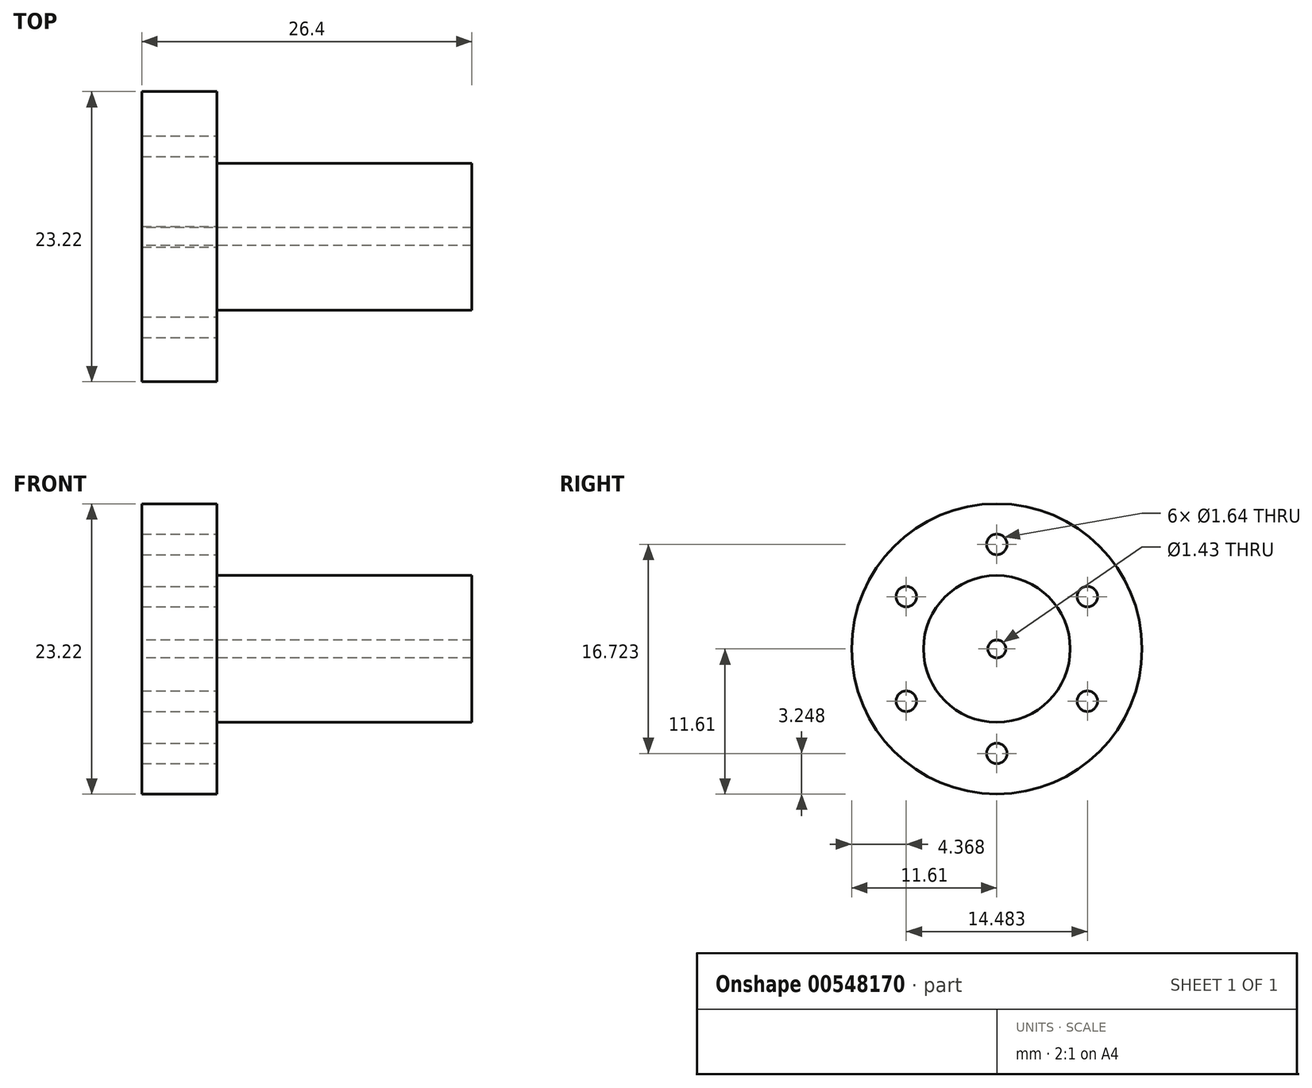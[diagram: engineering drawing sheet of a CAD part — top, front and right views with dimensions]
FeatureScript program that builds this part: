
annotation { "Feature Type Name" : "Feature", "Feature Type Description" : "" }
export const myFeature = defineFeature(function(context is Context, id is Id, definition is map)
    precondition{}
    {
        {
            var Q0;
            Q0=qCreatedBy(makeId("Front.planeOp"),FACE);
            var sketch = newSketch(context, id + "F0", { "sketchPlane" : qUnion([Q0])});
            skLineSegment(sketch, "E0", {"start": v(-9.4, 11.6) * mm, "end": v(-9.4, 0.72) * mm});
            skLineSegment(sketch, "E1", {"start": v(-9.4, 0.72) * mm, "end": v(17, 0.72) * mm});
            skLineSegment(sketch, "E2", {"start": v(17, 0.72) * mm, "end": v(17, 5.87) * mm});
            skLineSegment(sketch, "E3", {"start": v(17, 5.87) * mm, "end": v(-3.4, 5.87) * mm});
            skLineSegment(sketch, "E4", {"start": v(-3.4, 5.87) * mm, "end": v(-3.4, 11.6) * mm});
            skLineSegment(sketch, "E5", {"start": v(-3.4, 11.6) * mm, "end": v(-9.4, 11.6) * mm});
            skLineSegment(sketch, "E6", {"start": v(-18.4, 0) * mm, "end": v(18.59, 0) * mm, "construction": true});
            skSolve(sketch);
        }
        {
            var Q0;
            Q0 = qSketchRegion(id + "F0", true);
            var Q1;
            Q1=sQuery(id+"F0.wireOp",EDGE,"E6");
            revolve(context, id + "F1", {"entities" : qUnion([Q0]), "axis" : qUnion([Q1]), "revolveType" : RevolveType.FULL});
        }
        {
            var Q0;
            Q0=makeQuery(id+"F1.opRevolve","SWEPT_FACE",FACE,{"disambiguationData":[OSD([sQuery(id+"F0.wireOp",EDGE,"E2")])]});
            var sketch = newSketch(context, id + "F2", { "sketchPlane" : qUnion([Q0])});
            skSolve(sketch);
        }
        {
            var Q0;
            Q0=makeQuery(id+"F1.opRevolve","SWEPT_FACE",FACE,{"disambiguationData":[OSD([sQuery(id+"F0.wireOp",EDGE,"E4")])]});
            var sketch = newSketch(context, id + "F3", { "sketchPlane" : qUnion([Q0])});
            skLineSegment(sketch, "E7", {"start": v(0, 0) * mm, "end": v(0, 12.55) * mm, "construction": true});
            skCircle(sketch, "E8", {"center": v(0, 8.36) * mm, "radius": 0.82 * mm});
            skCircle(sketch, "E9.1.0", {"center": v(7.24, 4.18) * mm, "radius": 0.82 * mm});
            skCircle(sketch, "E9.2.0", {"center": v(7.24, -4.18) * mm, "radius": 0.82 * mm});
            skCircle(sketch, "E9.3.0", {"center": v(0, -8.36) * mm, "radius": 0.82 * mm});
            skCircle(sketch, "E9.4.0", {"center": v(-7.24, -4.18) * mm, "radius": 0.82 * mm});
            skCircle(sketch, "E9.5.0", {"center": v(-7.24, 4.18) * mm, "radius": 0.82 * mm});
            skPoint(sketch, "E9.center", {"position": v(0, 0) * mm});
            skLineSegment(sketch, "E9.anchor1", {"start": v(0, 0) * mm, "end": v(0, 8.36) * mm, "construction": true});
            skLineSegment(sketch, "E9.anchor2", {"start": v(0, 0) * mm, "end": v(-7.24, 4.18) * mm, "construction": true});
            skSolve(sketch);
        }
        {
            var Q0;
            Q0=makeQuery(id+"F3.imprint","IMPRINT",FACE,{"disambiguationData":[TD([[makeQuery(id+"F3.imprint","IMPRINT",EDGE,{"derivedFrom":sQuery(id+"F3.wireOp",EDGE,"E8")}),-1.0]])]});
            var sketch = newSketch(context, id + "F4", { "sketchPlane" : qUnion([Q0])});
            skSolve(sketch);
        }
        {
            var Q0;
            Q0=makeQuery(id+"F3.imprint","IMPRINT",FACE,{"disambiguationData":[TD([[makeQuery(id+"F3.imprint","IMPRINT",EDGE,{"derivedFrom":sQuery(id+"F3.wireOp",EDGE,"E9.5.0")}),1.0]])]});
            var Q1;
            Q1=makeQuery(id+"F3.imprint","IMPRINT",FACE,{"disambiguationData":[TD([[makeQuery(id+"F3.imprint","IMPRINT",EDGE,{"derivedFrom":sQuery(id+"F3.wireOp",EDGE,"E9.4.0")}),1.0]])]});
            var Q2;
            Q2=makeQuery(id+"F3.imprint","IMPRINT",FACE,{"disambiguationData":[TD([[makeQuery(id+"F3.imprint","IMPRINT",EDGE,{"derivedFrom":sQuery(id+"F3.wireOp",EDGE,"E9.3.0")}),1.0]])]});
            var Q3;
            Q3=makeQuery(id+"F3.imprint","IMPRINT",FACE,{"disambiguationData":[TD([[makeQuery(id+"F3.imprint","IMPRINT",EDGE,{"derivedFrom":sQuery(id+"F3.wireOp",EDGE,"E9.1.0")}),1.0]])]});
            var Q4;
            Q4=makeQuery(id+"F2.imprint","IMPRINT",FACE,{"disambiguationData":[TD([[makeQuery(id+"F2.imprint","IMPRINT",EDGE,{"derivedFrom":makeQuery(id+"F1.opRevolve","SWEPT_EDGE",EDGE,{"disambiguationData":[OSD([sQuery(id+"F0.wireOp",EDGE,"E1"),sQuery(id+"F0.wireOp",EDGE,"E2")])]})}),-1.0]])]});
            var Q5;
            Q5=makeQuery(id+"F3.imprint","IMPRINT",FACE,{"disambiguationData":[TD([[makeQuery(id+"F3.imprint","IMPRINT",EDGE,{"derivedFrom":sQuery(id+"F3.wireOp",EDGE,"E9.2.0")}),1.0]])]});
            var Q6;
            Q6=makeQuery(id+"F3.imprint","IMPRINT",FACE,{"disambiguationData":[TD([[makeQuery(id+"F3.imprint","IMPRINT",EDGE,{"derivedFrom":sQuery(id+"F3.wireOp",EDGE,"E8")}),1.0]])]});
            extrude(context, id + "F5", {"entities" : qUnion([Q0, Q1, Q2, Q3, Q4, Q5, Q6]), "operationType" : NewBodyOperationType.REMOVE, "endBound" : BoundingType.THROUGH_ALL, "oppositeDirection" : true, "depth" : 25 * mm, "offsetDistance" : 25 * mm});
        }
    });
